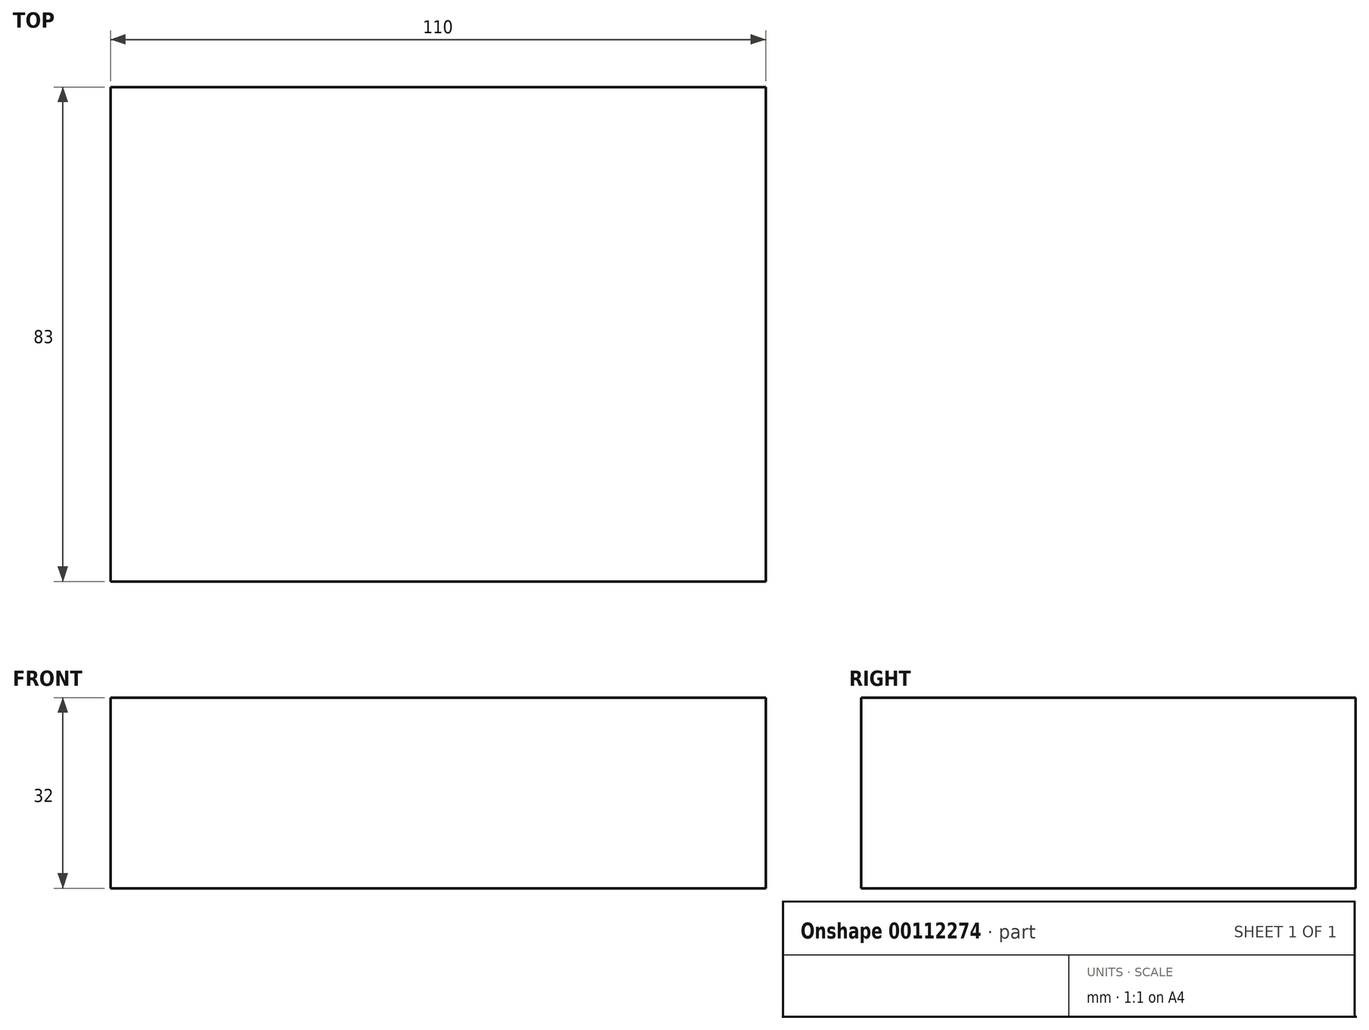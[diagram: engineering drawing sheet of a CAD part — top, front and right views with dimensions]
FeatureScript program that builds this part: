
annotation { "Feature Type Name" : "Feature", "Feature Type Description" : "" }
export const myFeature = defineFeature(function(context is Context, id is Id, definition is map)
    precondition{}
    {
        {
            var Q0;
            Q0=qCreatedBy(makeId("Top.planeOp"),FACE);
            var sketch = newSketch(context, id + "F0", { "sketchPlane" : qUnion([Q0])});
            skLineSegment(sketch, "E0.bottom", {"start": v(55, 41.5) * mm, "end": v(-55, 41.5) * mm});
            skLineSegment(sketch, "E0.top", {"start": v(55, -41.5) * mm, "end": v(-55, -41.5) * mm});
            skLineSegment(sketch, "E0.left", {"start": v(55, 41.5) * mm, "end": v(55, -41.5) * mm});
            skLineSegment(sketch, "E0.right", {"start": v(-55, 41.5) * mm, "end": v(-55, -41.5) * mm});
            skPoint(sketch, "E0.middle", {"position": v(0, 0) * mm});
            skSolve(sketch);
        }
        {
            var Q0;
            Q0=makeQuery(id+"F0.imprint","IMPRINT",FACE,{"disambiguationData":[TD([[makeQuery(id+"F0.imprint","IMPRINT",EDGE,{"derivedFrom":sQuery(id+"F0.wireOp",EDGE,"E0.bottom")}),1.0]])]});
            extrude(context, id + "F1", {"entities" : qUnion([Q0]), "depth" : 32 * mm});
        }
    });
